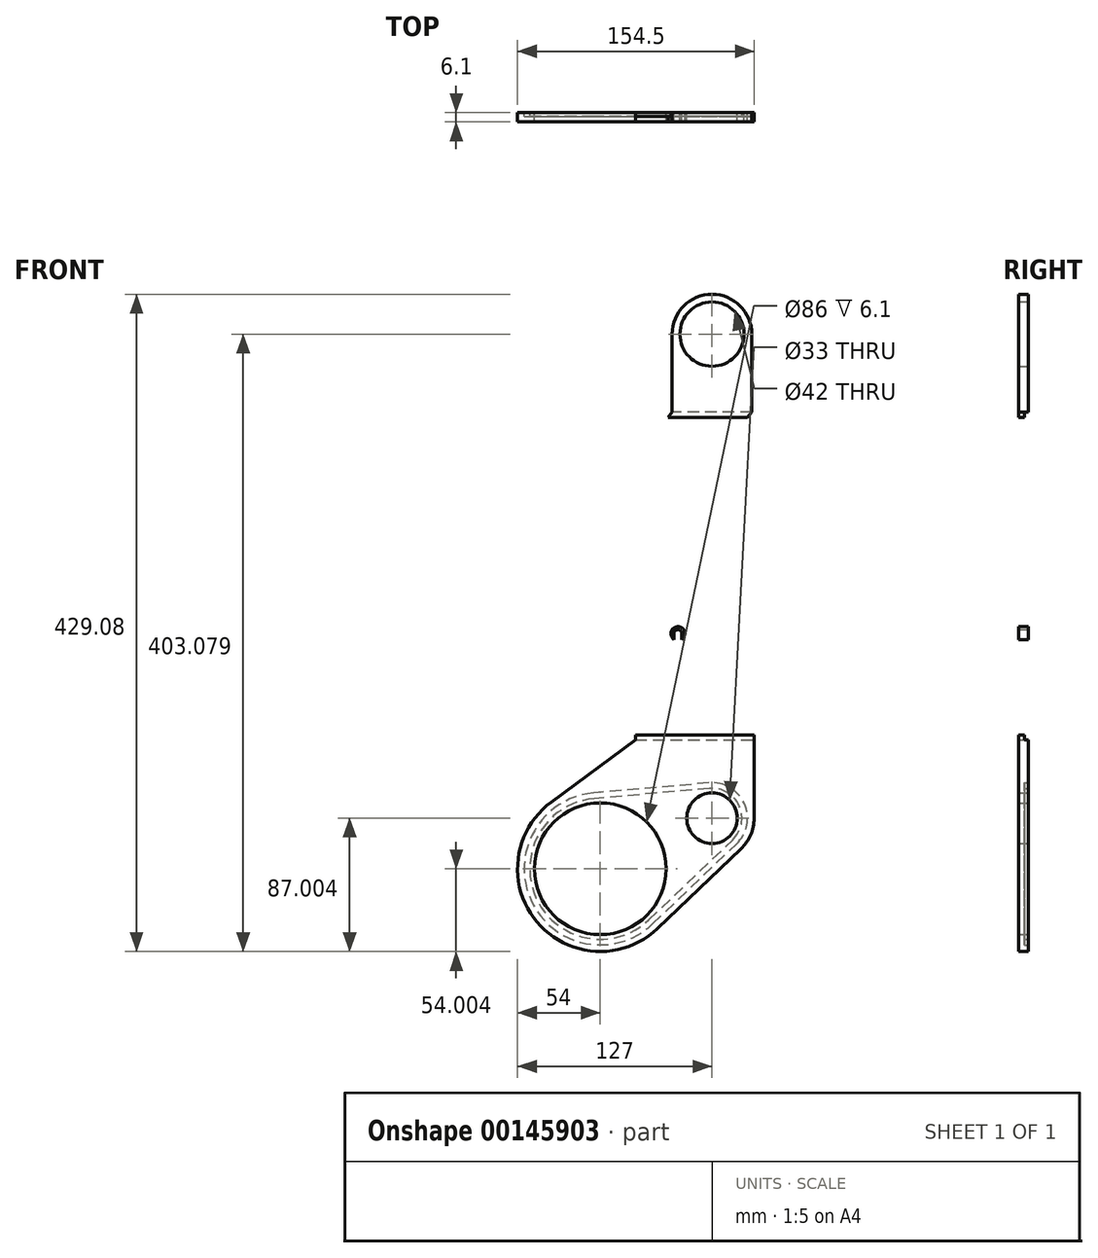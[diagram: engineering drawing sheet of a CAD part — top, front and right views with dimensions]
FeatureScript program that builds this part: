
annotation { "Feature Type Name" : "Feature", "Feature Type Description" : "" }
export const myFeature = defineFeature(function(context is Context, id is Id, definition is map)
    precondition{}
    {
        {
            var Q0;
            Q0=qCreatedBy(makeId("Front.planeOp"),FACE);
            var sketch = newSketch(context, id + "F0", { "sketchPlane" : qUnion([Q0])});
            skLineSegment(sketch, "E0.bottom", {"start": v(20, 66.9) * mm, "end": v(-20, 66.9) * mm});
            skLineSegment(sketch, "E0.top", {"start": v(20, -66.9) * mm, "end": v(-20, -66.9) * mm});
            skLineSegment(sketch, "E0.left", {"start": v(20, 66.9) * mm, "end": v(20, -66.9) * mm});
            skLineSegment(sketch, "E0.right", {"start": v(-20, 66.9) * mm, "end": v(-20, -66.9) * mm});
            skPoint(sketch, "E0.middle", {"position": v(0, 0) * mm});
            skLineSegment(sketch, "E1.bottom", {"start": v(20, -55.9) * mm, "end": v(76, -55.9) * mm});
            skLineSegment(sketch, "E1.top", {"start": v(20, 83.15) * mm, "end": v(76, 83.15) * mm});
            skLineSegment(sketch, "E1.left", {"start": v(20, -55.9) * mm, "end": v(20, 83.15) * mm});
            skLineSegment(sketch, "E1.right", {"start": v(76, -55.9) * mm, "end": v(76, 83.15) * mm});
            skLineSegment(sketch, "E2", {"start": v(0, 43.22) * mm, "end": v(0, -37.87) * mm, "construction": true});
            skCircle(sketch, "E3", {"center": v(68.75, 59.26) * mm, "radius": 3.5 * mm, "construction": true});
            skCircle(sketch, "E4", {"center": v(68.75, -33.17) * mm, "radius": 3.5 * mm, "construction": true});
            skCircle(sketch, "E5", {"center": v(50.75, 75.6) * mm, "radius": 2.5 * mm});
            skCircle(sketch, "E6", {"center": v(50.75, -48.4) * mm, "radius": 2.5 * mm});
            skLineSegment(sketch, "E7.MirrorCS", {"start": v(-20, 66.9) * mm, "end": v(20, 66.9) * mm});
            skLineSegment(sketch, "E8.MirrorCS", {"start": v(-20, -66.9) * mm, "end": v(20, -66.9) * mm});
            skCircle(sketch, "E9.MirrorC", {"center": v(-50.75, -48.4) * mm, "radius": 2.5 * mm});
            skCircle(sketch, "E10.MirrorC", {"center": v(-68.75, -33.17) * mm, "radius": 3.5 * mm, "construction": true});
            skLineSegment(sketch, "E11.MirrorCS", {"start": v(-20, -55.9) * mm, "end": v(-76, -55.9) * mm});
            skLineSegment(sketch, "E12.MirrorCS", {"start": v(-20, 83.15) * mm, "end": v(-76, 83.15) * mm});
            skCircle(sketch, "E13.MirrorC", {"center": v(-68.75, 59.26) * mm, "radius": 3.5 * mm, "construction": true});
            skCircle(sketch, "E14.MirrorC", {"center": v(-50.75, 75.6) * mm, "radius": 2.5 * mm});
            skLineSegment(sketch, "E15.MirrorCS", {"start": v(-76, -55.9) * mm, "end": v(-76, 83.15) * mm});
            skLineSegment(sketch, "E16.MirrorCS", {"start": v(-20, -55.9) * mm, "end": v(-20, 83.15) * mm});
            skLineSegment(sketch, "E17.bottom", {"start": v(150.22, -126.4) * mm, "end": v(-150.22, -126.4) * mm, "construction": true});
            skLineSegment(sketch, "E17.top", {"start": v(150.22, -146.43) * mm, "end": v(-150.22, -146.43) * mm, "construction": true});
            skLineSegment(sketch, "E17.left", {"start": v(150.22, -126.4) * mm, "end": v(150.22, -146.43) * mm, "construction": true});
            skLineSegment(sketch, "E17.right", {"start": v(-150.22, -126.4) * mm, "end": v(-150.22, -146.43) * mm, "construction": true});
            skPoint(sketch, "E17.middle", {"position": v(0, -136.42) * mm});
            skCircle(sketch, "E18", {"center": v(34.5, -28.92) * mm, "radius": 10 * mm, "construction": true});
            skCircle(sketch, "E19", {"center": v(34.5, 34.93) * mm, "radius": 10 * mm, "construction": true});
            skCircle(sketch, "E20.MirrorC", {"center": v(-34.5, 34.93) * mm, "radius": 10 * mm, "construction": true});
            skCircle(sketch, "E21.MirrorC", {"center": v(-34.5, -28.92) * mm, "radius": 10 * mm, "construction": true});
            skLineSegment(sketch, "E22", {"start": v(44.5, 64.55) * mm, "end": v(44.5, -50.82) * mm, "construction": true});
            skLineSegment(sketch, "E23.MirrorCS", {"start": v(-44.5, 64.55) * mm, "end": v(-44.5, -50.82) * mm, "construction": true});
            skSolve(sketch);
        }
        {
            var Q0;
            Q0=qCreatedBy(makeId("Front.planeOp"),FACE);
            var sketch = newSketch(context, id + "F1", { "sketchPlane" : qUnion([Q0])});
            skLineSegment(sketch, "E24", {"start": v(50.75, -48.4) * mm, "end": v(50.75, -2.9) * mm, "construction": true});
            skArc(sketch, "E25", {"start": v(53.35, -48.4) * mm, "mid": v(50.75, -51) * mm, "end": v(48.15, -48.4) * mm});
            skLineSegment(sketch, "E26", {"start": v(53.35, -48.4) * mm, "end": v(53.35, -23.41) * mm});
            skLineSegment(sketch, "E27", {"start": v(48.15, -48.4) * mm, "end": v(48.15, -25.65) * mm});
            skLineSegment(sketch, "E28", {"start": v(48.15, -25.65) * mm, "end": v(50.75, -25.65) * mm});
            skLineSegment(sketch, "E29.MirrorCS", {"start": v(48.15, -48.4) * mm, "end": v(48.15, -23.41) * mm});
            skLineSegment(sketch, "E30.MirrorCS", {"start": v(53.35, -48.4) * mm, "end": v(53.35, -25.65) * mm});
            skArc(sketch, "E31.MirrorCS", {"start": v(53.35, -2.9) * mm, "mid": v(50.75, -0.3) * mm, "end": v(48.15, -2.9) * mm});
            skLineSegment(sketch, "E32.MirrorCS", {"start": v(53.35, -2.9) * mm, "end": v(53.35, -27.89) * mm});
            skLineSegment(sketch, "E33.MirrorCS", {"start": v(48.15, -2.9) * mm, "end": v(48.15, -25.65) * mm});
            skLineSegment(sketch, "E34.MirrorCS", {"start": v(53.35, -2.9) * mm, "end": v(53.35, -25.65) * mm});
            skLineSegment(sketch, "E35.MirrorCS", {"start": v(48.15, -2.9) * mm, "end": v(48.15, -27.89) * mm});
            skLineSegment(sketch, "E36", {"start": v(50.75, 75.6) * mm, "end": v(50.75, 121.1) * mm, "construction": true});
            skArc(sketch, "E37", {"start": v(53.35, 75.6) * mm, "mid": v(50.75, 73) * mm, "end": v(48.15, 75.6) * mm});
            skLineSegment(sketch, "E38", {"start": v(53.35, 75.6) * mm, "end": v(53.35, 98.52) * mm});
            skLineSegment(sketch, "E39", {"start": v(50.75, 98.35) * mm, "end": v(53.35, 98.52) * mm});
            skLineSegment(sketch, "E40", {"start": v(48.15, 75.6) * mm, "end": v(48.15, 98.35) * mm});
            skLineSegment(sketch, "E41", {"start": v(48.15, 98.35) * mm, "end": v(50.75, 98.35) * mm});
            skLineSegment(sketch, "E42.MirrorCS", {"start": v(48.15, 75.6) * mm, "end": v(48.15, 98.52) * mm});
            skLineSegment(sketch, "E43.MirrorCS", {"start": v(53.35, 75.6) * mm, "end": v(53.35, 98.35) * mm});
            skArc(sketch, "E44.MirrorCS", {"start": v(48.15, 75.6) * mm, "mid": v(50.75, 73) * mm, "end": v(53.35, 75.6) * mm});
            skLineSegment(sketch, "E45.MirrorCS", {"start": v(50.75, 98.35) * mm, "end": v(53.35, 98.17) * mm});
            skArc(sketch, "E46.MirrorCS", {"start": v(53.35, 121.1) * mm, "mid": v(50.75, 123.7) * mm, "end": v(48.15, 121.1) * mm});
            skLineSegment(sketch, "E47.MirrorCS", {"start": v(53.35, 121.1) * mm, "end": v(53.35, 98.17) * mm});
            skLineSegment(sketch, "E48.MirrorCS", {"start": v(48.15, 121.1) * mm, "end": v(48.15, 98.35) * mm});
            skArc(sketch, "E49.MirrorCS", {"start": v(48.15, 121.1) * mm, "mid": v(50.75, 123.7) * mm, "end": v(53.35, 121.1) * mm});
            skLineSegment(sketch, "E50.MirrorCS", {"start": v(53.35, 121.1) * mm, "end": v(53.35, 98.35) * mm});
            skLineSegment(sketch, "E51.MirrorCS", {"start": v(48.15, 121.1) * mm, "end": v(48.15, 98.17) * mm});
            skLineSegment(sketch, "E52", {"start": v(63.25, -38.59) * mm, "end": v(63.25, 97.46) * mm});
            skLineSegment(sketch, "E53", {"start": v(99, 141.7) * mm, "end": v(47, 141.7) * mm});
            skLineSegment(sketch, "E54", {"start": v(23, 110.63) * mm, "end": v(23, -72.38) * mm});
            skLineSegment(sketch, "E55", {"start": v(23, -72.38) * mm, "end": v(0, -72.38) * mm, "construction": true});
            skCircle(sketch, "E56", {"center": v(50.75, -2.9) * mm, "radius": 4.6 * mm});
            skCircle(sketch, "E57", {"center": v(50.75, -48.4) * mm, "radius": 4.6 * mm});
            skCircle(sketch, "E58", {"center": v(50.75, 75.6) * mm, "radius": 4.6 * mm});
            skCircle(sketch, "E59", {"center": v(50.75, 121.1) * mm, "radius": 4.6 * mm});
            skLineSegment(sketch, "E60", {"start": v(23, 110.63) * mm, "end": v(47, 141.7) * mm});
            skLineSegment(sketch, "E61.top", {"start": v(23, -68.9) * mm, "end": v(100.5, -68.9) * mm});
            skLineSegment(sketch, "E61.left", {"start": v(23, -72.38) * mm, "end": v(23, -68.9) * mm});
            skLineSegment(sketch, "E61.right", {"start": v(100.5, -72.38) * mm, "end": v(100.5, -68.9) * mm});
            skLineSegment(sketch, "E62.direction1", {"start": v(23, -72.38) * mm, "end": v(100.5, -72.38) * mm});
            skLineSegment(sketch, "E63", {"start": v(23, -72.38) * mm, "end": v(23, -72.38) * mm});
            skCircle(sketch, "E64", {"center": v(0, -156.38) * mm, "radius": 43 * mm});
            skCircle(sketch, "E65", {"center": v(73, -123.38) * mm, "radius": 16.5 * mm});
            skArc(sketch, "E66", {"start": v(-32.02, -112.9) * mm, "mid": v(-41.36, -191.1) * mm, "end": v(37.27, -195.45) * mm});
            skLineSegment(sketch, "E67", {"start": v(-32.02, -112.9) * mm, "end": v(23, -72.38) * mm});
            skLineSegment(sketch, "E68", {"start": v(37.27, -195.45) * mm, "end": v(91.98, -143.28) * mm});
            skArc(sketch, "E69", {"start": v(91.98, -143.28) * mm, "mid": v(98.28, -134.2) * mm, "end": v(100.5, -123.38) * mm});
            skLineSegment(sketch, "E70", {"start": v(100.5, -123.38) * mm, "end": v(100.5, -72.38) * mm});
            skLineSegment(sketch, "E71", {"start": v(100.5, -68.9) * mm, "end": v(63.25, -38.59) * mm});
            skArc(sketch, "E72", {"start": v(-4.34, -106.9) * mm, "mid": v(-45.26, -176.84) * mm, "end": v(34.28, -192.32) * mm});
            skArc(sketch, "E73", {"start": v(70.98, -100.29) * mm, "mid": v(94.12, -113.83) * mm, "end": v(89, -140.15) * mm});
            skLineSegment(sketch, "E74", {"start": v(34.28, -192.32) * mm, "end": v(89, -140.15) * mm});
            skLineSegment(sketch, "E75", {"start": v(70.98, -100.29) * mm, "end": v(-4.34, -106.9) * mm});
            skLineSegment(sketch, "E76.0", {"start": v(71.3, -103.95) * mm, "end": v(-4.02, -110.55) * mm});
            skArc(sketch, "E76.1", {"start": v(71.3, -103.95) * mm, "mid": v(90.77, -115.34) * mm, "end": v(86.46, -137.49) * mm});
            skLineSegment(sketch, "E76.2", {"start": v(31.75, -189.66) * mm, "end": v(86.46, -137.49) * mm});
            skArc(sketch, "E76.3", {"start": v(-4.02, -110.55) * mm, "mid": v(-41.92, -175.32) * mm, "end": v(31.75, -189.66) * mm});
            skCircle(sketch, "E77", {"center": v(73, 192.7) * mm, "radius": 21 * mm});
            skLineSegment(sketch, "E78", {"start": v(73, -123.38) * mm, "end": v(73, 192.7) * mm, "construction": true});
            skArc(sketch, "E79", {"start": v(99, 192.7) * mm, "mid": v(73, 218.7) * mm, "end": v(47, 192.7) * mm});
            skLineSegment(sketch, "E80", {"start": v(47, 192.7) * mm, "end": v(47, 141.7) * mm});
            skLineSegment(sketch, "E81", {"start": v(99, 192.7) * mm, "end": v(99, 141.7) * mm});
            skLineSegment(sketch, "E82", {"start": v(44.5, -61.05) * mm, "end": v(44.5, 233) * mm, "construction": true});
            skLineSegment(sketch, "E83", {"start": v(63.25, 97.46) * mm, "end": v(99, 141.7) * mm});
            skLineSegment(sketch, "E84", {"start": v(44.32, 138.22) * mm, "end": v(96.2, 138.22) * mm});
            skSolve(sketch);
        }
        {
            var Q0;
            {var subQ30=sQuery(id+"F1.wireOp",EDGE,"E32.MirrorCS");Q0=makeQuery(id+"F1.imprint","IMPRINT",FACE,{"disambiguationData":[TD([[makeQuery(id+"F1.imprint","IMPRINT",EDGE,{"derivedFrom":subQ30}),1.0]])]});}
            var Q1;
            Q1=makeQuery(id+"F1.imprint","IMPRINT",FACE,{"disambiguationData":[TD([[makeQuery(id+"F1.imprint","IMPRINT",EDGE,{"derivedFrom":sQuery(id+"F1.wireOp",EDGE,"E53")}),-1.0]])]});
            var Q2;
            {var subQ0=sQuery(id+"F1.wireOp",EDGE,"E53");Q2=makeQuery(id+"F1.imprint","IMPRINT",FACE,{"disambiguationData":[TD([[makeQuery(id+"F1.imprint","IMPRINT",EDGE,{"derivedFrom":subQ0}),1.0]])]});}
            var Q3;
            Q3=makeQuery(id+"F1.imprint","IMPRINT",FACE,{"disambiguationData":[TD([[makeQuery(id+"F1.imprint","IMPRINT",EDGE,{"derivedFrom":sQuery(id+"F1.wireOp",EDGE,"E61.top")}),-1.0]])]});
            var Q4;
            Q4=makeQuery(id+"F1.imprint","IMPRINT",FACE,{"disambiguationData":[TD([[makeQuery(id+"F1.imprint","IMPRINT",EDGE,{"derivedFrom":sQuery(id+"F1.wireOp",EDGE,"E62.direction1")}),-1.0]])]});
            var Q5;
            Q5=makeQuery(id+"F1.imprint","IMPRINT",FACE,{"disambiguationData":[TD([[makeQuery(id+"F1.imprint","IMPRINT",EDGE,{"derivedFrom":sQuery(id+"F1.wireOp",EDGE,"E64")}),-1.0]])]});
            var Q6;
            Q6=makeQuery(id+"F1.imprint","IMPRINT",FACE,{"disambiguationData":[TD([[makeQuery(id+"F1.imprint","IMPRINT",EDGE,{"derivedFrom":sQuery(id+"F1.wireOp",EDGE,"E72")}),1.0]])]});
            extrude(context, id + "F2", {"entities" : qUnion([Q0, Q1, Q2, Q3, Q4, Q5, Q6]), "depth" : 6.1 * mm});
        }
        {
            var Q0;
            {var subQ0=sQuery(id+"F1.wireOp",EDGE,"E53");Q0=makeQuery(id+"F1.imprint","IMPRINT",FACE,{"disambiguationData":[TD([[makeQuery(id+"F1.imprint","IMPRINT",EDGE,{"derivedFrom":subQ0}),1.0]])]});}
            var Q1;
            Q1=makeQuery(id+"F1.imprint","IMPRINT",FACE,{"disambiguationData":[TD([[makeQuery(id+"F1.imprint","IMPRINT",EDGE,{"derivedFrom":sQuery(id+"F1.wireOp",EDGE,"E61.top")}),-1.0]])]});
            var Q2;
            Q2=makeQuery(id+"F1.imprint","IMPRINT",FACE,{"disambiguationData":[TD([[makeQuery(id+"F1.imprint","IMPRINT",EDGE,{"derivedFrom":sQuery(id+"F1.wireOp",EDGE,"E72")}),1.0]])]});
            extrude(context, id + "F3", {"entities" : qUnion([Q0, Q1, Q2]), "operationType" : NewBodyOperationType.REMOVE, "depth" : 2.5 * mm});
        }
    });
